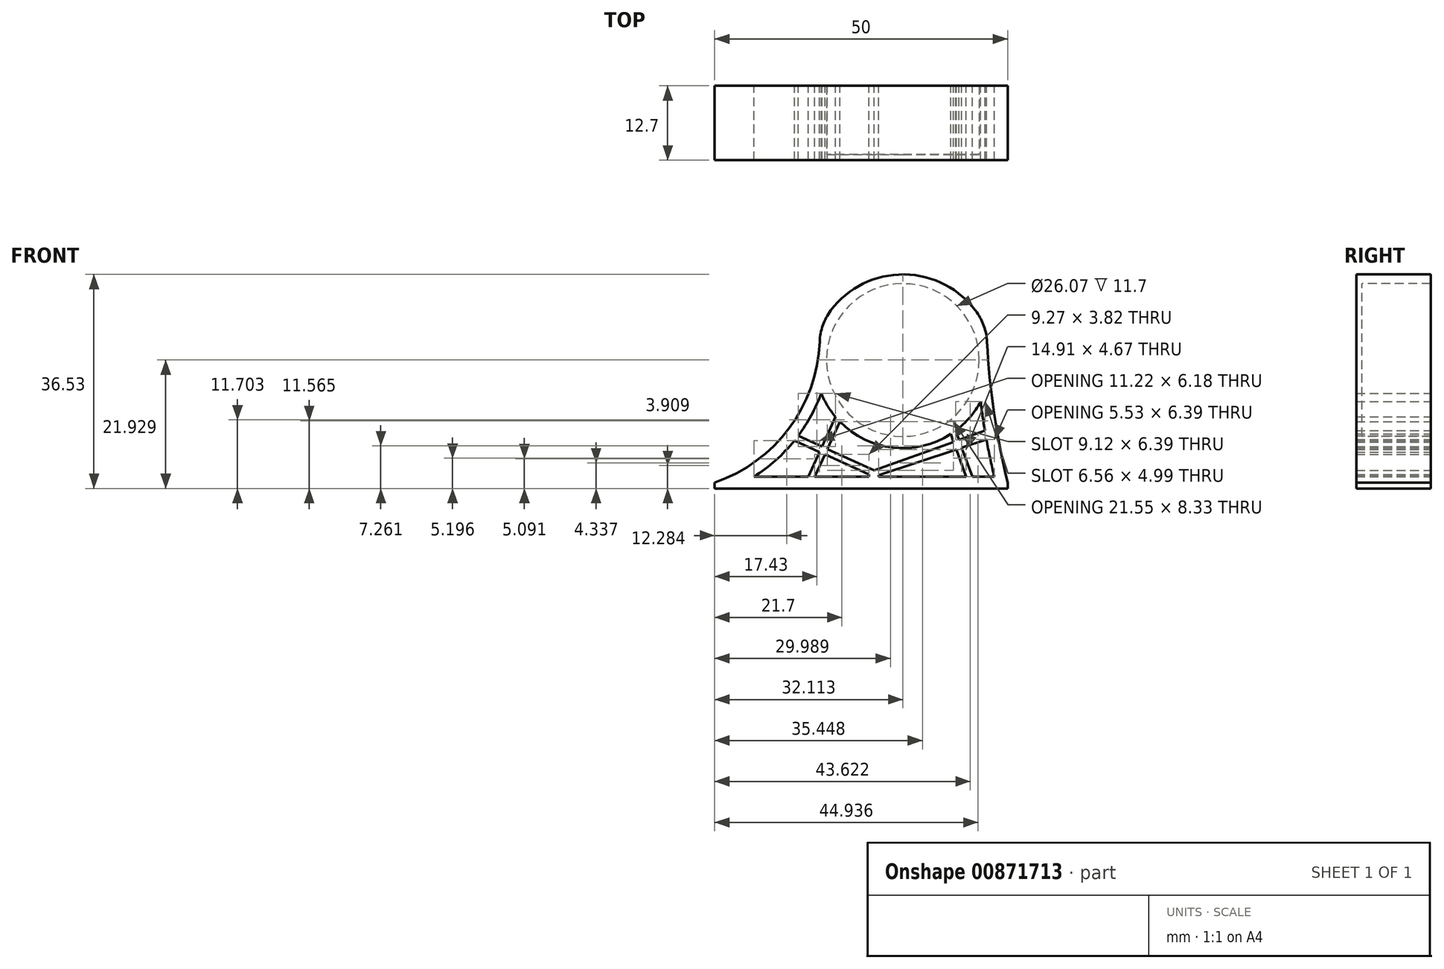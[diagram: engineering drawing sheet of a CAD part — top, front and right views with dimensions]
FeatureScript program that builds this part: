
annotation { "Feature Type Name" : "Feature", "Feature Type Description" : "" }
export const myFeature = defineFeature(function(context is Context, id is Id, definition is map)
    precondition{}
    {
        {
            var Q0;
            Q0=qCreatedBy(makeId("Front.planeOp"),FACE);
            var sketch = newSketch(context, id + "F0", { "sketchPlane" : qUnion([Q0])});
            skLineSegment(sketch, "E0.bottom", {"start": v(25, -0.5) * mm, "end": v(-25, -0.5) * mm});
            skLineSegment(sketch, "E0.left", {"start": v(25, -0.5) * mm, "end": v(25, 0.5) * mm});
            skLineSegment(sketch, "E0.right", {"start": v(-25, -0.5) * mm, "end": v(-25, 0.5) * mm});
            skPoint(sketch, "E0.middle", {"position": v(0, 0) * mm});
            skCircle(sketch, "E1", {"center": v(7.11, 21.43) * mm, "radius": 13.04 * mm});
            skArc(sketch, "E2", {"start": v(-25, 0.5) * mm, "mid": v(-11.73, 10.58) * mm, "end": v(-7.09, 26.59) * mm});
            skArc(sketch, "E3", {"start": v(21.4, 26.59) * mm, "mid": v(22.51, 13.45) * mm, "end": v(25, 0.5) * mm});
            skArc(sketch, "E4", {"start": v(21.4, 26.59) * mm, "mid": v(7.16, 36.03) * mm, "end": v(-7.09, 26.59) * mm});
            skSolve(sketch);
        }
        {
            var Q0;
            Q0 = qSketchRegion(id + "F0", true);
            var Q1;
            Q1=makeQuery(id+"F0.imprint","IMPRINT",FACE,{"disambiguationData":[TD([[makeQuery(id+"F0.imprint","IMPRINT",EDGE,{"derivedFrom":sQuery(id+"F0.wireOp",EDGE,"E1")}),1.0]])]});
            extrude(context, id + "F1", {"entities" : qUnion([Q0, Q1]), "depth" : 1 * mm, "offsetDistance" : 25 * mm});
        }
        {
            var Q0;
            Q0=makeQuery(id+"F0.imprint","IMPRINT",FACE,{"disambiguationData":[TD([[makeQuery(id+"F0.imprint","IMPRINT",EDGE,{"derivedFrom":sQuery(id+"F0.wireOp",EDGE,"E0.bottom")}),-1.0]])]});
            extrude(context, id + "F2", {"entities" : qUnion([Q0]), "operationType" : NewBodyOperationType.ADD, "oppositeDirection" : true, "depth" : 11.7 * mm, "offsetDistance" : 25 * mm});
        }
        {
            var Q0;
            Q0=makeQuery(id+"F2.opExtrude","CAP_FACE",FACE,{"disambiguationData":[OSD([sQuery(id+"F0.wireOp",EDGE,"E0.bottom"),sQuery(id+"F0.wireOp",EDGE,"E0.left"),sQuery(id+"F0.wireOp",EDGE,"E0.right"),sQuery(id+"F0.wireOp",EDGE,"E1"),sQuery(id+"F0.wireOp",EDGE,"E2"),sQuery(id+"F0.wireOp",EDGE,"E3"),sQuery(id+"F0.wireOp",EDGE,"E4")])],"isStart":false});
            var sketch = newSketch(context, id + "F3", { "sketchPlane" : qUnion([Q0])});
            skArc(sketch, "E5.0", {"start": v(6.82, 15.76) * mm, "mid": v(-6.33, 6.41) * mm, "end": v(-20.38, 14.34) * mm});
            skArc(sketch, "E6.0", {"start": v(18.32, 1.5) * mm, "mid": v(11.4, 7.68) * mm, "end": v(6.82, 15.76) * mm});
            skArc(sketch, "E7.0", {"start": v(-20.38, 14.34) * mm, "mid": v(-21.37, 7.9) * mm, "end": v(-22.7, 1.5) * mm});
            skLineSegment(sketch, "E8.0", {"start": v(-22.7, 1.5) * mm, "end": v(18.32, 1.5) * mm});
            skLineSegment(sketch, "E9", {"start": v(-21.37, 7.9) * mm, "end": v(-17.17, 6.5) * mm});
            skLineSegment(sketch, "E10", {"start": v(-1.33, 1.89) * mm, "end": v(6.2, 5.32) * mm});
            skLineSegment(sketch, "E11", {"start": v(11.4, 7.68) * mm, "end": v(10.76, 8.5) * mm});
            skLineSegment(sketch, "E12", {"start": v(10.76, 8.5) * mm, "end": v(6.7, 6.64) * mm});
            skLineSegment(sketch, "E13", {"start": v(-2.19, 2.6) * mm, "end": v(-15.76, 7.45) * mm});
            skLineSegment(sketch, "E14", {"start": v(4.38, 11.73) * mm, "end": v(6.7, 6.64) * mm});
            skLineSegment(sketch, "E15", {"start": v(3.65, 10.92) * mm, "end": v(5.78, 6.23) * mm});
            skLineSegment(sketch, "E16.trimOffspring", {"start": v(5.78, 6.23) * mm, "end": v(-2.19, 2.6) * mm});
            skLineSegment(sketch, "E17.trimOffspring", {"start": v(7.1, 5.73) * mm, "end": v(9.03, 1.5) * mm});
            skLineSegment(sketch, "E18.trimOffspring", {"start": v(7.1, 5.73) * mm, "end": v(11.4, 7.68) * mm});
            skLineSegment(sketch, "E19.trimOffspring", {"start": v(6.2, 5.32) * mm, "end": v(7.94, 1.5) * mm});
            skLineSegment(sketch, "E20", {"start": v(-16.13, 9.4) * mm, "end": v(-16.7, 7.79) * mm});
            skLineSegment(sketch, "E21", {"start": v(-15.28, 8.8) * mm, "end": v(-15.76, 7.45) * mm});
            skLineSegment(sketch, "E22.trimOffspring", {"start": v(-16.7, 7.79) * mm, "end": v(-21.12, 9.36) * mm});
            skLineSegment(sketch, "E23.trimOffspring", {"start": v(-17.17, 6.5) * mm, "end": v(-18.96, 1.5) * mm});
            skLineSegment(sketch, "E24.trimOffspring", {"start": v(-16.22, 6.17) * mm, "end": v(-17.9, 1.5) * mm});
            skLineSegment(sketch, "E25.trimOffspring", {"start": v(-16.22, 6.17) * mm, "end": v(-3, 1.77) * mm});
            skLineSegment(sketch, "E26", {"start": v(-3, 1.77) * mm, "end": v(-3, 1.5) * mm});
            skLineSegment(sketch, "E27", {"start": v(-1.33, 1.89) * mm, "end": v(-1.33, 1.5) * mm});
            skPoint(sketch, "E28.orphan", {"position": v(-2.19, 1.5) * mm});
            skSolve(sketch);
        }
        {
            var Q0;
            {var subQ3=sQuery(id+"F3.wireOp",EDGE,"E9");Q0=makeQuery(id+"F3.imprint","IMPRINT",FACE,{"disambiguationData":[TD([[makeQuery(id+"F3.imprint","IMPRINT",EDGE,{"derivedFrom":subQ3}),-1.0]])]});}
            var Q1;
            {var subQ3=sQuery(id+"F3.wireOp",EDGE,"E20");Q1=makeQuery(id+"F3.imprint","IMPRINT",FACE,{"disambiguationData":[TD([[makeQuery(id+"F3.imprint","IMPRINT",EDGE,{"derivedFrom":subQ3}),-1.0]])]});}
            var Q2;
            Q2=makeQuery(id+"F3.imprint","IMPRINT",FACE,{"disambiguationData":[TD([[makeQuery(id+"F3.imprint","IMPRINT",EDGE,{"derivedFrom":sQuery(id+"F3.wireOp",EDGE,"E13")}),-1.0]])]});
            var Q3;
            {var subQ2=sQuery(id+"F3.wireOp",EDGE,"E24.trimOffspring");Q3=makeQuery(id+"F3.imprint","IMPRINT",FACE,{"disambiguationData":[TD([[makeQuery(id+"F3.imprint","IMPRINT",EDGE,{"derivedFrom":subQ2}),1.0]])]});}
            var Q4;
            {var subQ0=sQuery(id+"F3.wireOp",EDGE,"E10");Q4=makeQuery(id+"F3.imprint","IMPRINT",FACE,{"disambiguationData":[TD([[makeQuery(id+"F3.imprint","IMPRINT",EDGE,{"derivedFrom":subQ0}),-1.0]])]});}
            var Q5;
            {var subQ4=sQuery(id+"F3.wireOp",EDGE,"E17.trimOffspring");Q5=makeQuery(id+"F3.imprint","IMPRINT",FACE,{"disambiguationData":[TD([[makeQuery(id+"F3.imprint","IMPRINT",EDGE,{"derivedFrom":subQ4}),1.0]])]});}
            var Q6;
            {var subQ4=sQuery(id+"F3.wireOp",EDGE,"E12");Q6=makeQuery(id+"F3.imprint","IMPRINT",FACE,{"disambiguationData":[TD([[makeQuery(id+"F3.imprint","IMPRINT",EDGE,{"derivedFrom":subQ4}),-1.0]])]});}
            extrude(context, id + "F4", {"entities" : qUnion([Q0, Q1, Q2, Q3, Q4, Q5, Q6]), "operationType" : NewBodyOperationType.REMOVE, "oppositeDirection" : true, "depth" : 25 * mm, "offsetDistance" : 25 * mm});
        }
        {
            var Q0;
            {var subQ0=sQuery(id+"F0.wireOp",EDGE,"E4");var subQ1=sQuery(id+"F0.wireOp",EDGE,"E2");Q0=makeQuery(id+"F2.boolean.opBoolean","MERGE",EDGE,{"derivedFrom":[makeQuery(id+"F1.opExtrude","SWEPT_EDGE",EDGE,{"disambiguationData":[OSD([subQ1,subQ0])]}),makeQuery(id+"F2.opExtrude","SWEPT_EDGE",EDGE,{"disambiguationData":[OSD([subQ1,subQ0])]})]});}
            var Q1;
            {var subQ0=sQuery(id+"F0.wireOp",EDGE,"E4");var subQ1=sQuery(id+"F0.wireOp",EDGE,"E3");Q1=makeQuery(id+"F2.boolean.opBoolean","MERGE",EDGE,{"derivedFrom":[makeQuery(id+"F1.opExtrude","SWEPT_EDGE",EDGE,{"disambiguationData":[OSD([subQ1,subQ0])]}),makeQuery(id+"F2.opExtrude","SWEPT_EDGE",EDGE,{"disambiguationData":[OSD([subQ1,subQ0])]})]});}
            fillet(context, id + "F5", {"entities" : qUnion([Q0, Q1]), "radius" : 9.45 * mm, "tangentPropagation" : true, "allowEdgeOverflow" : false});
        }
    });
